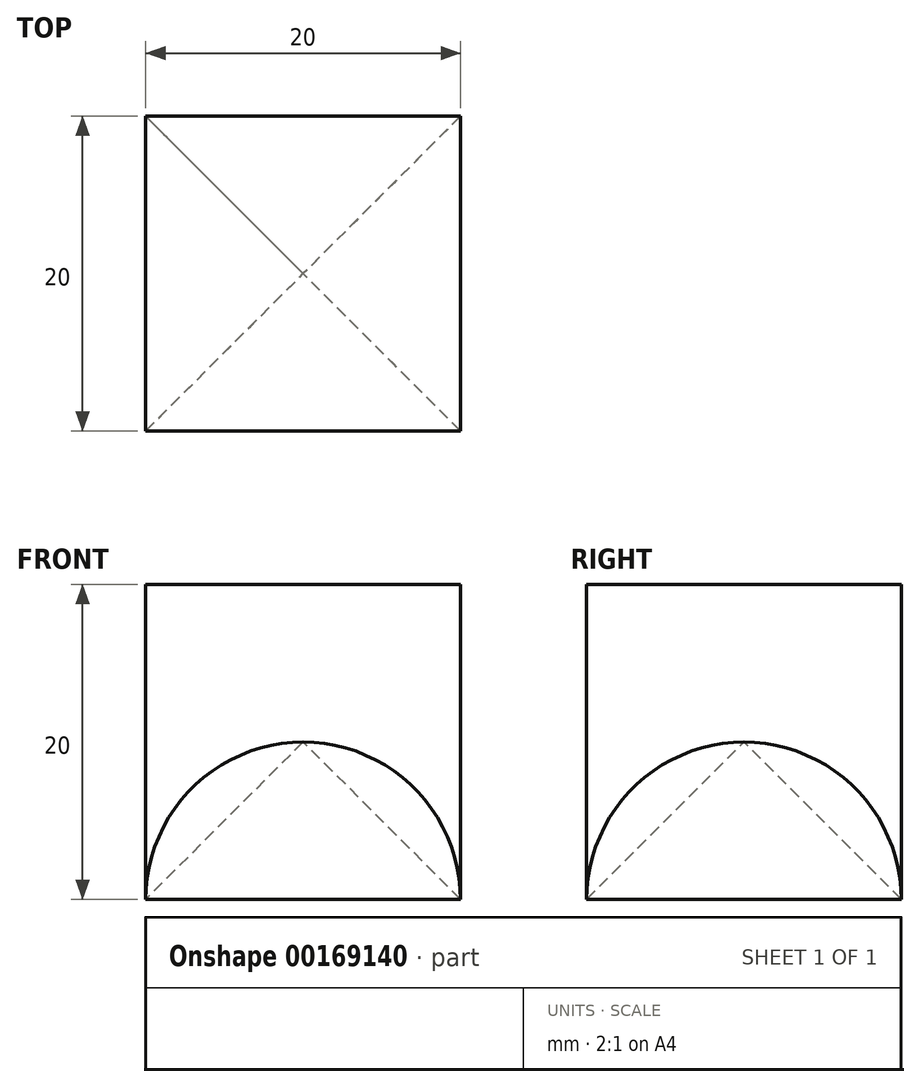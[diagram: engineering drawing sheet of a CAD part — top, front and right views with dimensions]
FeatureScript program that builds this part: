
annotation { "Feature Type Name" : "Feature", "Feature Type Description" : "" }
export const myFeature = defineFeature(function(context is Context, id is Id, definition is map)
    precondition{}
    {
        {
            var Q0;
            Q0=qCreatedBy(makeId("Top.planeOp"),FACE);
            var sketch = newSketch(context, id + "F0", { "sketchPlane" : qUnion([Q0])});
            skLineSegment(sketch, "E0.bottom", {"start": v(-10.07, 12.22) * mm, "end": v(9.93, 12.22) * mm});
            skLineSegment(sketch, "E0.top", {"start": v(-10.07, -7.78) * mm, "end": v(9.93, -7.78) * mm});
            skLineSegment(sketch, "E0.left", {"start": v(-10.07, 12.22) * mm, "end": v(-10.07, -7.78) * mm});
            skLineSegment(sketch, "E0.right", {"start": v(9.93, 12.22) * mm, "end": v(9.93, -7.78) * mm});
            skSolve(sketch);
        }
        {
            var Q0;
            Q0=makeQuery(id+"F0.imprint","IMPRINT",FACE,{"disambiguationData":[TD([[makeQuery(id+"F0.imprint","IMPRINT",EDGE,{"derivedFrom":sQuery(id+"F0.wireOp",EDGE,"E0.bottom")}),-1.0]])]});
            var Q1;
            Q1 = qSketchRegion(id + "F0", true);
            extrude(context, id + "F1", {"entities" : qUnion([Q0, Q1]), "depth" : 20 * mm});
        }
        {
            var Q0;
            Q0 = qSketchRegion(id + "F0", true);
            extrude(context, id + "F2", {"entities" : qUnion([Q0]), "depth" : 10 * mm});
        }
        {
            var Q0;
            Q0=makeQuery(id+"F2.opExtrude","CAP_FACE",FACE,{"disambiguationData":[OSD([sQuery(id+"F0.wireOp",EDGE,"E0.bottom"),sQuery(id+"F0.wireOp",EDGE,"E0.top"),sQuery(id+"F0.wireOp",EDGE,"E0.left"),sQuery(id+"F0.wireOp",EDGE,"E0.right")])],"isStart":false});
            chamfer(context, id + "F3", {"entities" : qUnion([Q0]), "width" : 10 * mm, "tangentPropagation" : true});
        }
        {
            var Q0;
            Q0 = qSketchRegion(id + "F0", true);
            extrude(context, id + "F4", {"entities" : qUnion([Q0]), "depth" : 10 * mm});
        }
        {
            var Q0;
            Q0=makeQuery(id+"F4.opExtrude","CAP_FACE",FACE,{"disambiguationData":[OSD([sQuery(id+"F0.wireOp",EDGE,"E0.bottom"),sQuery(id+"F0.wireOp",EDGE,"E0.top"),sQuery(id+"F0.wireOp",EDGE,"E0.left"),sQuery(id+"F0.wireOp",EDGE,"E0.right")])],"isStart":false});
            fillet(context, id + "F5", {"entities" : qUnion([Q0]), "radius" : 10 * mm, "tangentPropagation" : true, "allowEdgeOverflow" : false});
        }
    });
